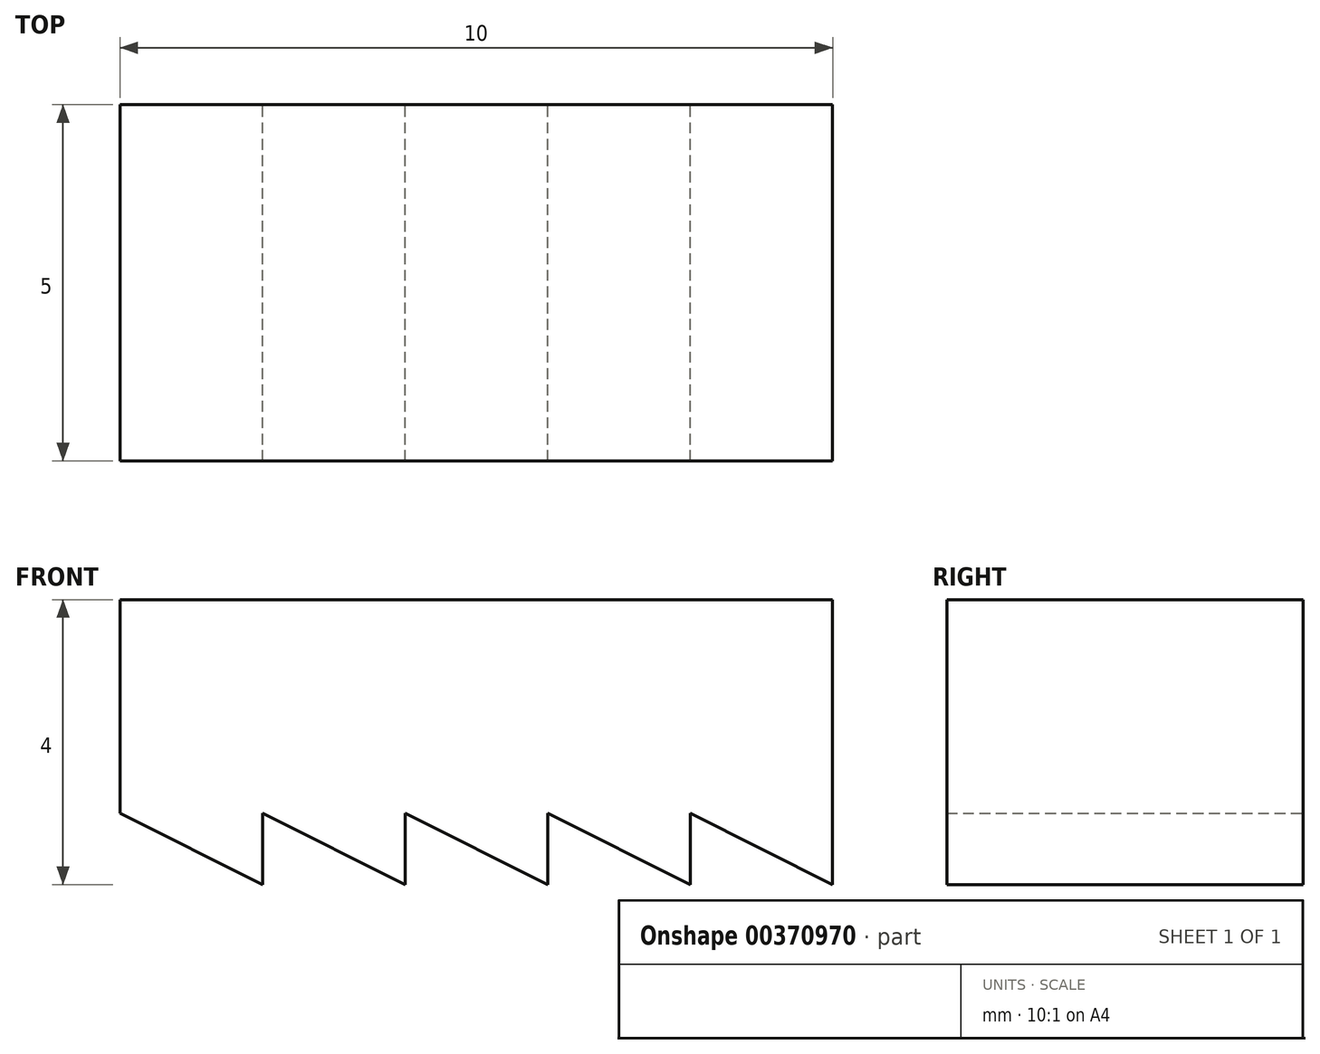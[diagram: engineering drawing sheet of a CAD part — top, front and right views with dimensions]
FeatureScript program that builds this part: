
annotation { "Feature Type Name" : "Feature", "Feature Type Description" : "" }
export const myFeature = defineFeature(function(context is Context, id is Id, definition is map)
    precondition{}
    {
        {
            var Q0;
            Q0=qCreatedBy(makeId("Front.planeOp"),FACE);
            var sketch = newSketch(context, id + "F0", { "sketchPlane" : qUnion([Q0])});
            skLineSegment(sketch, "E0", {"start": v(0, 0) * mm, "end": v(10, 0) * mm});
            skLineSegment(sketch, "E1", {"start": v(10, 0) * mm, "end": v(10, 4) * mm});
            skLineSegment(sketch, "E2", {"start": v(10, 4) * mm, "end": v(0, 4) * mm});
            skLineSegment(sketch, "E3", {"start": v(0, 4) * mm, "end": v(0, 0) * mm});
            skLineSegment(sketch, "E4", {"start": v(0, 0) * mm, "end": v(0, 1) * mm});
            skLineSegment(sketch, "E5", {"start": v(0, 0) * mm, "end": v(2, 0) * mm});
            skLineSegment(sketch, "E6", {"start": v(2, 0) * mm, "end": v(4, 0) * mm});
            skLineSegment(sketch, "E7", {"start": v(4, 0) * mm, "end": v(6, 0) * mm});
            skLineSegment(sketch, "E8", {"start": v(6, 0) * mm, "end": v(8, 0) * mm});
            skLineSegment(sketch, "E9", {"start": v(0, 1) * mm, "end": v(2, 0) * mm});
            skLineSegment(sketch, "E10", {"start": v(2, 0) * mm, "end": v(2, 1) * mm});
            skLineSegment(sketch, "E11", {"start": v(2, 1) * mm, "end": v(4, 0) * mm});
            skLineSegment(sketch, "E12", {"start": v(4, 1) * mm, "end": v(6, 0) * mm});
            skLineSegment(sketch, "E13", {"start": v(8, 1) * mm, "end": v(10, 0) * mm});
            skLineSegment(sketch, "E14", {"start": v(8, 1) * mm, "end": v(8, 0) * mm});
            skLineSegment(sketch, "E15", {"start": v(6, 1) * mm, "end": v(6, 0) * mm});
            skLineSegment(sketch, "E16", {"start": v(4, 1) * mm, "end": v(4, 0) * mm});
            skLineSegment(sketch, "E17", {"start": v(6, 1) * mm, "end": v(8, 0) * mm});
            skSolve(sketch);
        }
        {
            var Q0;
            Q0=makeQuery(id+"F0.imprint","IMPRINT",FACE,{"disambiguationData":[TD([[makeQuery(id+"F0.imprint","IMPRINT",EDGE,{"derivedFrom":sQuery(id+"F0.wireOp",EDGE,"E1")}),1.0]])]});
            extrude(context, id + "F1", {"entities" : qUnion([Q0]), "depth" : 5 * mm});
        }
    });
